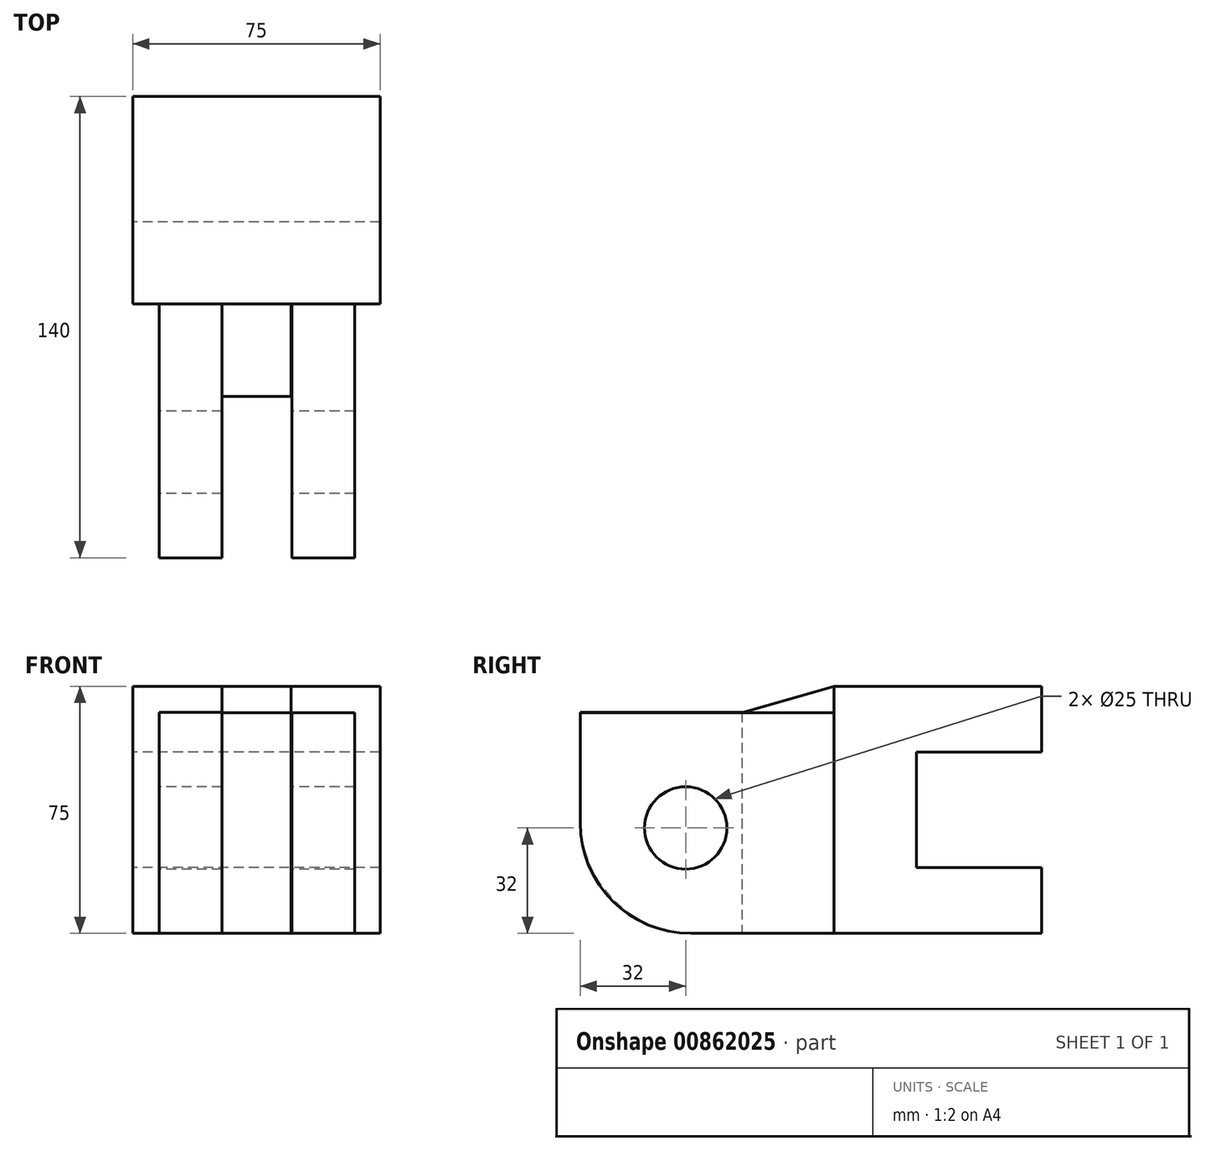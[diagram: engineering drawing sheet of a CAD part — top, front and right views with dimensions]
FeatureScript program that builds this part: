
annotation { "Feature Type Name" : "Feature", "Feature Type Description" : "" }
export const myFeature = defineFeature(function(context is Context, id is Id, definition is map)
    precondition{}
    {
        {
            var Q0;
            Q0=qCreatedBy(makeId("Right.planeOp"),FACE);
            var sketch = newSketch(context, id + "F0", { "sketchPlane" : qUnion([Q0])});
            skLineSegment(sketch, "E0", {"start": v(0, 0) * mm, "end": v(0, 75) * mm});
            skLineSegment(sketch, "E1", {"start": v(0, 75) * mm, "end": v(63, 75) * mm});
            skLineSegment(sketch, "E2", {"start": v(63, 75) * mm, "end": v(63, 55) * mm});
            skLineSegment(sketch, "E3", {"start": v(63, 55) * mm, "end": v(25, 55) * mm});
            skLineSegment(sketch, "E4", {"start": v(25, 55) * mm, "end": v(25, 20) * mm});
            skLineSegment(sketch, "E5", {"start": v(25, 20) * mm, "end": v(63, 20) * mm});
            skLineSegment(sketch, "E6", {"start": v(63, 20) * mm, "end": v(63, 0) * mm});
            skLineSegment(sketch, "E7", {"start": v(63, 0) * mm, "end": v(0, 0) * mm});
            skSolve(sketch);
        }
        {
            var Q0;
            Q0=makeQuery(id+"F0.imprint","IMPRINT",FACE,{"disambiguationData":[TD([[makeQuery(id+"F0.imprint","IMPRINT",EDGE,{"derivedFrom":sQuery(id+"F0.wireOp",EDGE,"E0")}),-1.0]])]});
            extrude(context, id + "F1", {"entities" : qUnion([Q0]), "depth" : 75 * mm, "offsetDistance" : 25 * mm});
        }
        {
            var Q0;
            Q0=makeQuery(id+"F1.opExtrude","SWEPT_FACE",FACE,{"disambiguationData":[OSD([sQuery(id+"F0.wireOp",EDGE,"E0")])]});
            var sketch = newSketch(context, id + "F2", { "sketchPlane" : qUnion([Q0])});
            skLineSegment(sketch, "E8", {"start": v(0, 75) * mm, "end": v(8, 75) * mm});
            skLineSegment(sketch, "E9", {"start": v(8, 75) * mm, "end": v(27, 75) * mm});
            skLineSegment(sketch, "E10", {"start": v(27, 75) * mm, "end": v(48, 75) * mm});
            skLineSegment(sketch, "E11", {"start": v(48, 75) * mm, "end": v(48, 0) * mm});
            skLineSegment(sketch, "E12", {"start": v(48, 0) * mm, "end": v(27, 0) * mm});
            skLineSegment(sketch, "E13", {"start": v(27, 0) * mm, "end": v(27, 75) * mm});
            skSolve(sketch);
        }
        {
            var Q0;
            Q0=makeQuery(id+"F2.imprint","IMPRINT",FACE,{"disambiguationData":[TD([[makeQuery(id+"F2.imprint","IMPRINT",EDGE,{"derivedFrom":sQuery(id+"F2.wireOp",EDGE,"E10")}),1.0]])]});
            extrude(context, id + "F3", {"entities" : qUnion([Q0]), "operationType" : NewBodyOperationType.ADD, "depth" : 28 * mm, "offsetDistance" : 25 * mm});
        }
        {
            var Q0;
            Q0=makeQuery(id+"F3.opExtrude","SWEPT_FACE",FACE,{"disambiguationData":[OSD([sQuery(id+"F2.wireOp",EDGE,"E13")])]});
            var sketch = newSketch(context, id + "F4", { "sketchPlane" : qUnion([Q0])});
            skLineSegment(sketch, "E14", {"start": v(28, 75) * mm, "end": v(28, 67) * mm});
            skLineSegment(sketch, "E15", {"start": v(28, 67) * mm, "end": v(0, 75) * mm});
            skLineSegment(sketch, "E16", {"start": v(0, 75) * mm, "end": v(28, 75) * mm});
            skSolve(sketch);
        }
        {
            var Q0;
            Q0=makeQuery(id+"F4.imprint","IMPRINT",FACE,{"disambiguationData":[TD([[makeQuery(id+"F4.imprint","IMPRINT",EDGE,{"derivedFrom":sQuery(id+"F4.wireOp",EDGE,"E14")}),1.0]])]});
            extrude(context, id + "F5", {"entities" : qUnion([Q0]), "operationType" : NewBodyOperationType.REMOVE, "oppositeDirection" : true, "depth" : 50.8 * mm, "offsetDistance" : 25 * mm});
        }
        {
            var Q0;
            Q0=qCreatedBy(makeId("Top.planeOp"),FACE);
            var sketch = newSketch(context, id + "F6", { "sketchPlane" : qUnion([Q0])});
            skLineSegment(sketch, "E17", {"start": v(48.3, 0) * mm, "end": v(67.3, 0) * mm});
            skLineSegment(sketch, "E18", {"start": v(67.3, 0) * mm, "end": v(67.3, -77) * mm});
            skLineSegment(sketch, "E19", {"start": v(67.3, -77) * mm, "end": v(48.3, -77) * mm});
            skLineSegment(sketch, "E20", {"start": v(48.3, 0) * mm, "end": v(48.3, -77) * mm});
            skSolve(sketch);
        }
        {
            var Q0;
            Q0=makeQuery(id+"F6.imprint","IMPRINT",FACE,{"disambiguationData":[TD([[makeQuery(id+"F6.imprint","IMPRINT",EDGE,{"derivedFrom":sQuery(id+"F6.wireOp",EDGE,"E17")}),-1.0]])]});
            extrude(context, id + "F7", {"entities" : qUnion([Q0]), "operationType" : NewBodyOperationType.ADD, "depth" : 75 * mm, "offsetDistance" : 25 * mm});
        }
        {
            var Q0;
            Q0=makeQuery(id+"F7.opExtrude","SWEPT_FACE",FACE,{"disambiguationData":[OSD([sQuery(id+"F6.wireOp",EDGE,"E20")])]});
            var sketch = newSketch(context, id + "F8", { "sketchPlane" : qUnion([Q0])});
            skLineSegment(sketch, "E21", {"start": v(0, 75) * mm, "end": v(77, 75) * mm});
            skLineSegment(sketch, "E22", {"start": v(77, 75) * mm, "end": v(77, 67) * mm});
            skLineSegment(sketch, "E23", {"start": v(77, 67) * mm, "end": v(27.78, 67) * mm});
            skLineSegment(sketch, "E24", {"start": v(27.78, 67) * mm, "end": v(0, 75) * mm});
            skSolve(sketch);
        }
        {
            var Q0;
            Q0=makeQuery(id+"F8.imprint","IMPRINT",FACE,{"disambiguationData":[TD([[makeQuery(id+"F8.imprint","IMPRINT",EDGE,{"derivedFrom":sQuery(id+"F8.wireOp",EDGE,"E21")}),-1.0]])]});
            extrude(context, id + "F9", {"entities" : qUnion([Q0]), "operationType" : NewBodyOperationType.REMOVE, "oppositeDirection" : true, "depth" : 38.6 * mm, "offsetDistance" : 25 * mm});
        }
        {
            var Q0;
            Q0=makeQuery(id+"F7.opExtrude","SWEPT_FACE",FACE,{"disambiguationData":[OSD([sQuery(id+"F6.wireOp",EDGE,"E18")])]});
            var sketch = newSketch(context, id + "F10", { "sketchPlane" : qUnion([Q0])});
            skLineSegment(sketch, "E25", {"start": v(-27.78, 67) * mm, "end": v(0, 67) * mm});
            skLineSegment(sketch, "E26", {"start": v(0, 67) * mm, "end": v(0, 75) * mm});
            skLineSegment(sketch, "E27", {"start": v(0, 75) * mm, "end": v(-27.78, 67) * mm});
            skSolve(sketch);
        }
        {
            var Q0;
            Q0=makeQuery(id+"F10.imprint","IMPRINT",FACE,{"disambiguationData":[TD([[makeQuery(id+"F10.imprint","IMPRINT",EDGE,{"derivedFrom":sQuery(id+"F10.wireOp",EDGE,"E25")}),1.0]])]});
            extrude(context, id + "F11", {"entities" : qUnion([Q0]), "operationType" : NewBodyOperationType.REMOVE, "oppositeDirection" : true, "depth" : 19 * mm, "offsetDistance" : 25 * mm});
        }
        {
            var Q0;
            Q0=qCreatedBy(makeId("Top.planeOp"),FACE);
            var sketch = newSketch(context, id + "F12", { "sketchPlane" : qUnion([Q0])});
            skLineSegment(sketch, "E28", {"start": v(0, 0) * mm, "end": v(8, 0) * mm});
            skLineSegment(sketch, "E29", {"start": v(8, 0) * mm, "end": v(8, -77) * mm});
            skLineSegment(sketch, "E30", {"start": v(8, -77) * mm, "end": v(27, -77) * mm});
            skLineSegment(sketch, "E31", {"start": v(27, -77) * mm, "end": v(27, 0) * mm});
            skLineSegment(sketch, "E32", {"start": v(27, 0) * mm, "end": v(8, 0) * mm});
            skSolve(sketch);
        }
        {
            var Q0;
            Q0=makeQuery(id+"F12.imprint","IMPRINT",FACE,{"disambiguationData":[TD([[makeQuery(id+"F12.imprint","IMPRINT",EDGE,{"derivedFrom":sQuery(id+"F12.wireOp",EDGE,"E29")}),1.0]])]});
            extrude(context, id + "F13", {"entities" : qUnion([Q0]), "operationType" : NewBodyOperationType.ADD, "depth" : 77 * mm, "offsetDistance" : 25 * mm});
        }
        {
            var Q0;
            Q0=makeQuery(id+"F13.opExtrude","SWEPT_FACE",FACE,{"disambiguationData":[OSD([sQuery(id+"F12.wireOp",EDGE,"E30")])]});
            var sketch = newSketch(context, id + "F14", { "sketchPlane" : qUnion([Q0])});
            skLineSegment(sketch, "E33", {"start": v(27, 67.06) * mm, "end": v(8, 67.06) * mm});
            skLineSegment(sketch, "E34", {"start": v(8, 67.06) * mm, "end": v(8, 77) * mm});
            skLineSegment(sketch, "E35", {"start": v(8, 77) * mm, "end": v(27, 77) * mm});
            skLineSegment(sketch, "E36", {"start": v(27, 77) * mm, "end": v(27, 67.06) * mm});
            skSolve(sketch);
        }
        {
            var Q0;
            Q0=makeQuery(id+"F14.imprint","IMPRINT",FACE,{"disambiguationData":[TD([[makeQuery(id+"F14.imprint","IMPRINT",EDGE,{"derivedFrom":sQuery(id+"F14.wireOp",EDGE,"E33")}),-1.0]])]});
            extrude(context, id + "F15", {"entities" : qUnion([Q0]), "operationType" : NewBodyOperationType.REMOVE, "oppositeDirection" : true, "depth" : 77 * mm, "offsetDistance" : 25 * mm});
        }
        {
            var Q0;
            Q0=makeQuery(id+"F13.opExtrude","SWEPT_FACE",FACE,{"disambiguationData":[OSD([sQuery(id+"F12.wireOp",EDGE,"E29")])]});
            var sketch = newSketch(context, id + "F16", { "sketchPlane" : qUnion([Q0])});
            skLineSegment(sketch, "E37", {"start": v(0, 0) * mm, "end": v(45, 0) * mm});
            skLineSegment(sketch, "E38", {"start": v(45, 0) * mm, "end": v(45, 32) * mm});
            skCircle(sketch, "E39", {"center": v(45, 32) * mm, "radius": 12.5 * mm});
            skSolve(sketch);
        }
        {
            var Q0;
            Q0=makeQuery(id+"F16.imprint","IMPRINT",FACE,{"disambiguationData":[TD([[makeQuery(id+"F16.imprint","IMPRINT",EDGE,{"derivedFrom":sQuery(id+"F16.wireOp",EDGE,"E39")}),1.0]])]});
            extrude(context, id + "F17", {"entities" : qUnion([Q0]), "operationType" : NewBodyOperationType.REMOVE, "oppositeDirection" : true, "depth" : 75.4 * mm, "offsetDistance" : 25 * mm});
        }
        {
            var Q0;
            Q0=makeQuery(id+"F15.boolean.opBoolean","COPY",EDGE,{"derivedFrom":makeQuery(id+"F15.opExtrude","CAP_EDGE",EDGE,{"disambiguationData":[OSD([sQuery(id+"F14.wireOp",EDGE,"E33")])],"isStart":true})});
            var Q1;
            Q1=makeQuery(id+"F13.opExtrude","CAP_EDGE",EDGE,{"disambiguationData":[OSD([sQuery(id+"F12.wireOp",EDGE,"E30")])],"isStart":true});
            fillet(context, id + "F18", {"entities" : qUnion([Q0, Q1]), "radius" : 34.52 * mm, "tangentPropagation" : true, "allowEdgeOverflow" : false});
        }
        {
            var Q0;
            Q0=makeQuery(id+"F9.boolean.opBoolean","COPY",EDGE,{"derivedFrom":makeQuery(id+"F9.opExtrude","SWEPT_EDGE",EDGE,{"disambiguationData":[OSD([sQuery(id+"F6.wireOp",EDGE,"E19"),sQuery(id+"F6.wireOp",EDGE,"E20"),sQuery(id+"F8.wireOp",EDGE,"E22"),sQuery(id+"F8.wireOp",EDGE,"E23")])]})});
            var Q1;
            Q1=makeQuery(id+"F7.opExtrude","CAP_EDGE",EDGE,{"disambiguationData":[OSD([sQuery(id+"F6.wireOp",EDGE,"E19")])],"isStart":true});
            fillet(context, id + "F19", {"entities" : qUnion([Q0, Q1]), "radius" : 33.56 * mm, "tangentPropagation" : true, "allowEdgeOverflow" : false});
        }
    });
